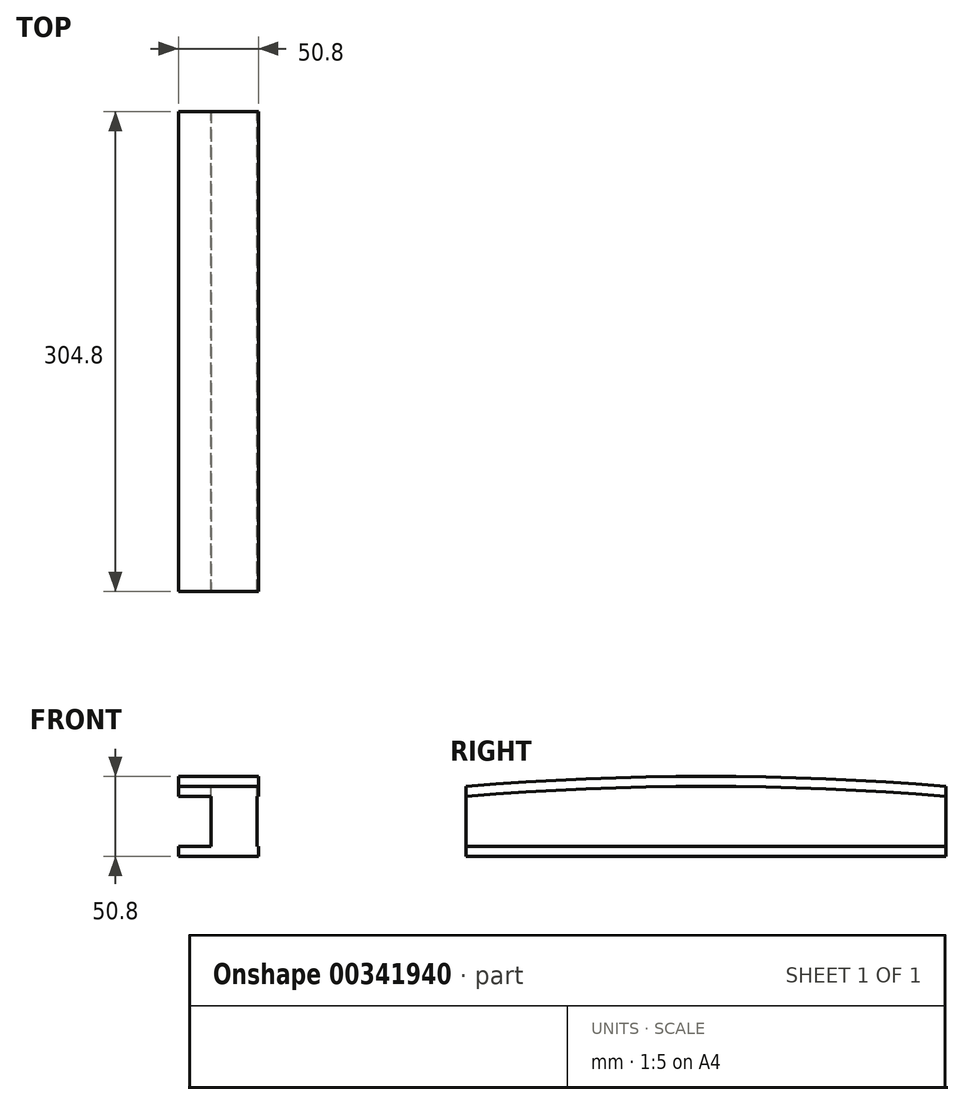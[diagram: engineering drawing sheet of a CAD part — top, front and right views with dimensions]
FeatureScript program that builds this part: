
annotation { "Feature Type Name" : "Feature", "Feature Type Description" : "" }
export const myFeature = defineFeature(function(context is Context, id is Id, definition is map)
    precondition{}
    {
        {
            var Q0;
            Q0=qCreatedBy(makeId("Right.planeOp"),FACE);
            var sketch = newSketch(context, id + "F0", { "sketchPlane" : qUnion([Q0])});
            skLineSegment(sketch, "E0", {"start": v(0, 0) * mm, "end": v(-304.8, 0) * mm});
            skLineSegment(sketch, "E1.left", {"start": v(-304.8, 0) * mm, "end": v(-304.8, 44.45) * mm});
            skLineSegment(sketch, "E1.right", {"start": v(0, 0) * mm, "end": v(0, 44.45) * mm});
            skLineSegment(sketch, "E2", {"start": v(-304.8, 0) * mm, "end": v(-304.8, 6.35) * mm});
            skLineSegment(sketch, "E3", {"start": v(0, 0) * mm, "end": v(0, 6.35) * mm});
            skArc(sketch, "E4", {"start": v(0, 44.45) * mm, "mid": v(-152.4, 50.8) * mm, "end": v(-304.8, 44.45) * mm});
            skPoint(sketch, "E5.orphan", {"position": v(-304.8, 50.8) * mm});
            skPoint(sketch, "E6.orphan", {"position": v(0, 50.8) * mm});
            skLineSegment(sketch, "E7", {"start": v(-304.8, 44.45) * mm, "end": v(-304.8, 38.1) * mm});
            skLineSegment(sketch, "E8", {"start": v(0, 44.45) * mm, "end": v(0, 38.1) * mm});
            skArc(sketch, "E9", {"start": v(0, 38.1) * mm, "mid": v(-152.4, 44.45) * mm, "end": v(-304.8, 38.1) * mm});
            skPoint(sketch, "E10.endSnap0", {"position": v(-152.4, 0) * mm});
            skLineSegment(sketch, "E11", {"start": v(-304.8, 6.35) * mm, "end": v(0, 6.35) * mm});
            skSolve(sketch);
        }
        {
            var Q0;
            Q0=makeQuery(id+"F0.imprint","IMPRINT",FACE,{"disambiguationData":[TD([[makeQuery(id+"F0.imprint","IMPRINT",EDGE,{"derivedFrom":sQuery(id+"F0.wireOp",EDGE,"E1.left")}),-1.0]])]});
            var Q1;
            Q1=makeQuery(id+"F0.imprint","IMPRINT",FACE,{"disambiguationData":[TD([[makeQuery(id+"F0.imprint","IMPRINT",EDGE,{"derivedFrom":sQuery(id+"F0.wireOp",EDGE,"E4")}),1.0]])]});
            var Q2;
            Q2=makeQuery(id+"F0.imprint","IMPRINT",FACE,{"disambiguationData":[TD([[makeQuery(id+"F0.imprint","IMPRINT",EDGE,{"derivedFrom":sQuery(id+"F0.wireOp",EDGE,"E0")}),-1.0]])]});
            extrude(context, id + "F1", {"entities" : qUnion([Q0, Q1, Q2]), "depth" : 50.8 * mm});
        }
        {
            var Q0;
            Q0=makeQuery(id+"F1.opExtrude","CAP_FACE",FACE,{"disambiguationData":[OSD([sQuery(id+"F0.wireOp",EDGE,"E0"),sQuery(id+"F0.wireOp",EDGE,"E1.left"),sQuery(id+"F0.wireOp",EDGE,"E1.right"),sQuery(id+"F0.wireOp",EDGE,"E2"),sQuery(id+"F0.wireOp",EDGE,"E3"),sQuery(id+"F0.wireOp",EDGE,"E4"),sQuery(id+"F0.wireOp",EDGE,"E7"),sQuery(id+"F0.wireOp",EDGE,"E8")])],"isStart":false});
            var sketch = newSketch(context, id + "F2", { "sketchPlane" : qUnion([Q0])});
            skLineSegment(sketch, "E12", {"start": v(0, 44.45) * mm, "end": v(0, 38.1) * mm});
            skLineSegment(sketch, "E13", {"start": v(-304.8, 44.45) * mm, "end": v(-304.8, 38.1) * mm});
            skLineSegment(sketch, "E14", {"start": v(-304.8, 0) * mm, "end": v(-304.8, 6.35) * mm});
            skLineSegment(sketch, "E15", {"start": v(0, 0) * mm, "end": v(0, 6.35) * mm});
            skPoint(sketch, "E16.endSnap0", {"position": v(-152.4, 0) * mm});
            skArc(sketch, "E17", {"start": v(0, 38.1) * mm, "mid": v(-152.4, 44.45) * mm, "end": v(-304.8, 38.1) * mm});
            skLineSegment(sketch, "E18.bottom", {"start": v(-304.8, 0) * mm, "end": v(0, 0) * mm});
            skLineSegment(sketch, "E18.top", {"start": v(-304.8, 6.35) * mm, "end": v(0, 6.35) * mm});
            skSolve(sketch);
        }
        {
            var Q0;
            {var subQ0=sQuery(id+"F2.wireOp",EDGE,"E17");Q0=makeQuery(id+"F2.imprint","IMPRINT",FACE,{"disambiguationData":[TD([[makeQuery(id+"F2.imprint","IMPRINT",EDGE,{"derivedFrom":subQ0}),1.0]])]});}
            extrude(context, id + "F3", {"entities" : qUnion([Q0]), "operationType" : NewBodyOperationType.REMOVE, "oppositeDirection" : true, "depth" : ((2 - (3 / 8)) / 2) * mm});
        }
        {
            var Q0;
            Q0=makeQuery(id+"F1.opExtrude","CAP_FACE",FACE,{"disambiguationData":[OSD([sQuery(id+"F0.wireOp",EDGE,"E0"),sQuery(id+"F0.wireOp",EDGE,"E1.left"),sQuery(id+"F0.wireOp",EDGE,"E1.right"),sQuery(id+"F0.wireOp",EDGE,"E2"),sQuery(id+"F0.wireOp",EDGE,"E3"),sQuery(id+"F0.wireOp",EDGE,"E4"),sQuery(id+"F0.wireOp",EDGE,"E7"),sQuery(id+"F0.wireOp",EDGE,"E8")])],"isStart":true});
            var sketch = newSketch(context, id + "F4", { "sketchPlane" : qUnion([Q0])});
            skLineSegment(sketch, "E19", {"start": v(304.8, 44.45) * mm, "end": v(304.8, 38.1) * mm});
            skLineSegment(sketch, "E20", {"start": v(304.8, 0) * mm, "end": v(304.8, 6.35) * mm});
            skLineSegment(sketch, "E21", {"start": v(0, 44.45) * mm, "end": v(0, 38.1) * mm});
            skLineSegment(sketch, "E22", {"start": v(0, 0) * mm, "end": v(0, 6.35) * mm});
            skPoint(sketch, "E23.endSnap0", {"position": v(152.4, 0) * mm});
            skArc(sketch, "E24", {"start": v(304.8, 38.1) * mm, "mid": v(152.4, 44.45) * mm, "end": v(0, 38.1) * mm});
            skLineSegment(sketch, "E25.bottom", {"start": v(0, 0) * mm, "end": v(304.8, 0) * mm});
            skLineSegment(sketch, "E25.top", {"start": v(0, 6.35) * mm, "end": v(304.8, 6.35) * mm});
            skSolve(sketch);
        }
        {
            var Q0;
            {var subQ0=sQuery(id+"F4.wireOp",EDGE,"E24");Q0=makeQuery(id+"F4.imprint","IMPRINT",FACE,{"disambiguationData":[TD([[makeQuery(id+"F4.imprint","IMPRINT",EDGE,{"derivedFrom":subQ0}),1.0]])]});}
            extrude(context, id + "F5", {"entities" : qUnion([Q0]), "operationType" : NewBodyOperationType.REMOVE, "oppositeDirection" : true, "depth" : 20.65 * mm});
        }
    });
